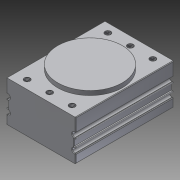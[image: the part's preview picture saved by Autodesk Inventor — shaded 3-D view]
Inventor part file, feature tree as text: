
AUTODESK INVENTOR PART (.ipt)
format: ipt  version: 2014 SP1 (Build 180222100, 222)  size: 220,672 bytes
history: native  units: in
note: dims shown in document units (in); Inventor stores cm internally (conversion verified against a paired STEP export)
features: thread x6, extrude x3, sketch x2, fillet x1, mirror x1
ambient origin geometry x8: Origin, YZ Plane, XZ Plane, XY Plane, X Axis, Y Axis, Z Axis, Center Point
bodies: Solid1 (feature_tree)
feature tree (13):
  extrude  "Extrusion1"  Depth=1.75in
  fillet  "Fillet1"  Radius=0.05in
  mirror  "Mirror1"
  sketch  "Sketch2"  dims[d5=1.5in d6=4.25in d7=0.0in d8=0.075in d9=0.05in d10=0.025in d11=0.6875in d12=0.475in d13=2.8in d14=0.375in d16=0.25in d17=1.1811in d19=0.975in d20=0.7874in d22=3.5in d25=4.25in d27=0.5in d28=2.95in d29=4.5in d30=0.0in d31=0.1875in d32=0.0in d33=1.0in d34=0.0in d35=1.0in d36=0.0in d37=1.0in d38=0.0in d39=1.0in d40=0.0in d41=1.0in d42=0.0in d43=1.0in d44=0.0in]
  extrude  "Extrusion2"  Depth=4.25in TaperAngle=0.0deg
  extrude  "Extrusion3"  Depth=0.075in
  thread  "Thread1"  [1 undecoded]
  thread  "Thread2"  [1 undecoded]
  thread  "Thread3"  [1 undecoded]
  thread  "Thread4"  [1 undecoded]
  thread  "Thread5"  [1 undecoded]
  thread  "Thread6"  [1 undecoded]
  sketch  "Sketch1"  dims[d0=0.1in d1=1.75in d4=0.05in]
note: 6 required parameter values undecoded (feature->parameter linkage not recoverable at this tier; creation-order binding heuristic only, values carry confidence <= 0.55)
